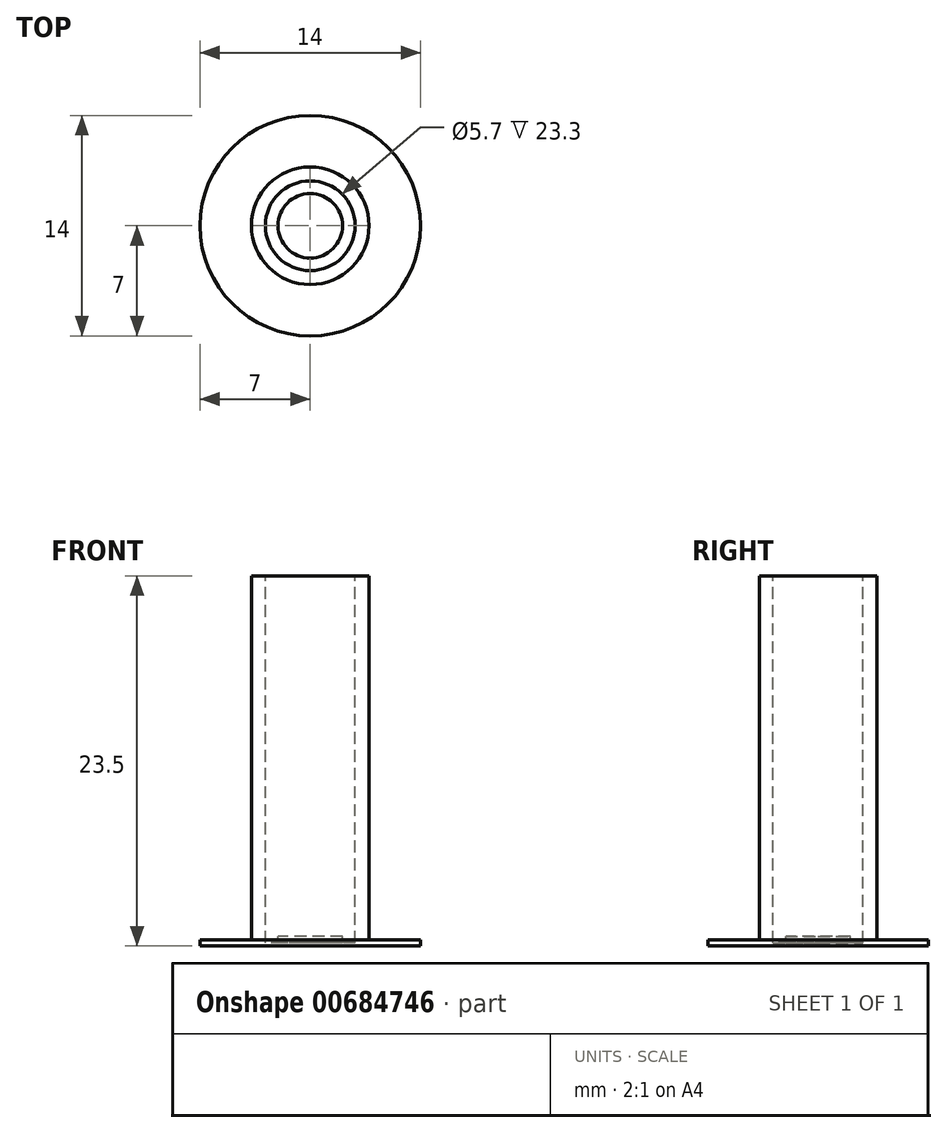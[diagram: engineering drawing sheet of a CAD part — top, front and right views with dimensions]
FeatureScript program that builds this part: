
annotation { "Feature Type Name" : "Feature", "Feature Type Description" : "" }
export const myFeature = defineFeature(function(context is Context, id is Id, definition is map)
    precondition{}
    {
        {
            var Q0;
            Q0=qCreatedBy(makeId("Front.planeOp"),FACE);
            var sketch = newSketch(context, id + "F0", { "sketchPlane" : qUnion([Q0])});
            skLineSegment(sketch, "E0", {"start": v(0, 0.6) * mm, "end": v(0, 0) * mm});
            skLineSegment(sketch, "E1", {"start": v(0, 0) * mm, "end": v(7, 0) * mm});
            skLineSegment(sketch, "E2", {"start": v(2.85, 23.5) * mm, "end": v(3.74, 23.5) * mm});
            skLineSegment(sketch, "E3", {"start": v(3.74, 23.5) * mm, "end": v(3.74, 0.4) * mm});
            skLineSegment(sketch, "E4", {"start": v(0, 0.6) * mm, "end": v(2.05, 0.6) * mm});
            skLineSegment(sketch, "E5", {"start": v(2.05, 0.6) * mm, "end": v(2.05, 0.2) * mm});
            skLineSegment(sketch, "E6", {"start": v(2.05, 0.2) * mm, "end": v(2.85, 0.2) * mm});
            skLineSegment(sketch, "E7", {"start": v(2.85, 0.2) * mm, "end": v(2.85, 23.5) * mm});
            skLineSegment(sketch, "E8", {"start": v(7, 0) * mm, "end": v(7, 0.4) * mm});
            skLineSegment(sketch, "E9", {"start": v(7, 0.4) * mm, "end": v(3.74, 0.4) * mm});
            skSolve(sketch);
        }
        {
            var Q0;
            Q0=qSketchRegion(id+"F0",true);
            var Q1;
            Q1=sQuery(id+"F0.wireOp",EDGE,"E0");
            revolve(context, id + "F1", {"entities" : qUnion([Q0]), "axis" : qUnion([Q1]), "revolveType" : RevolveType.FULL});
        }
    });
